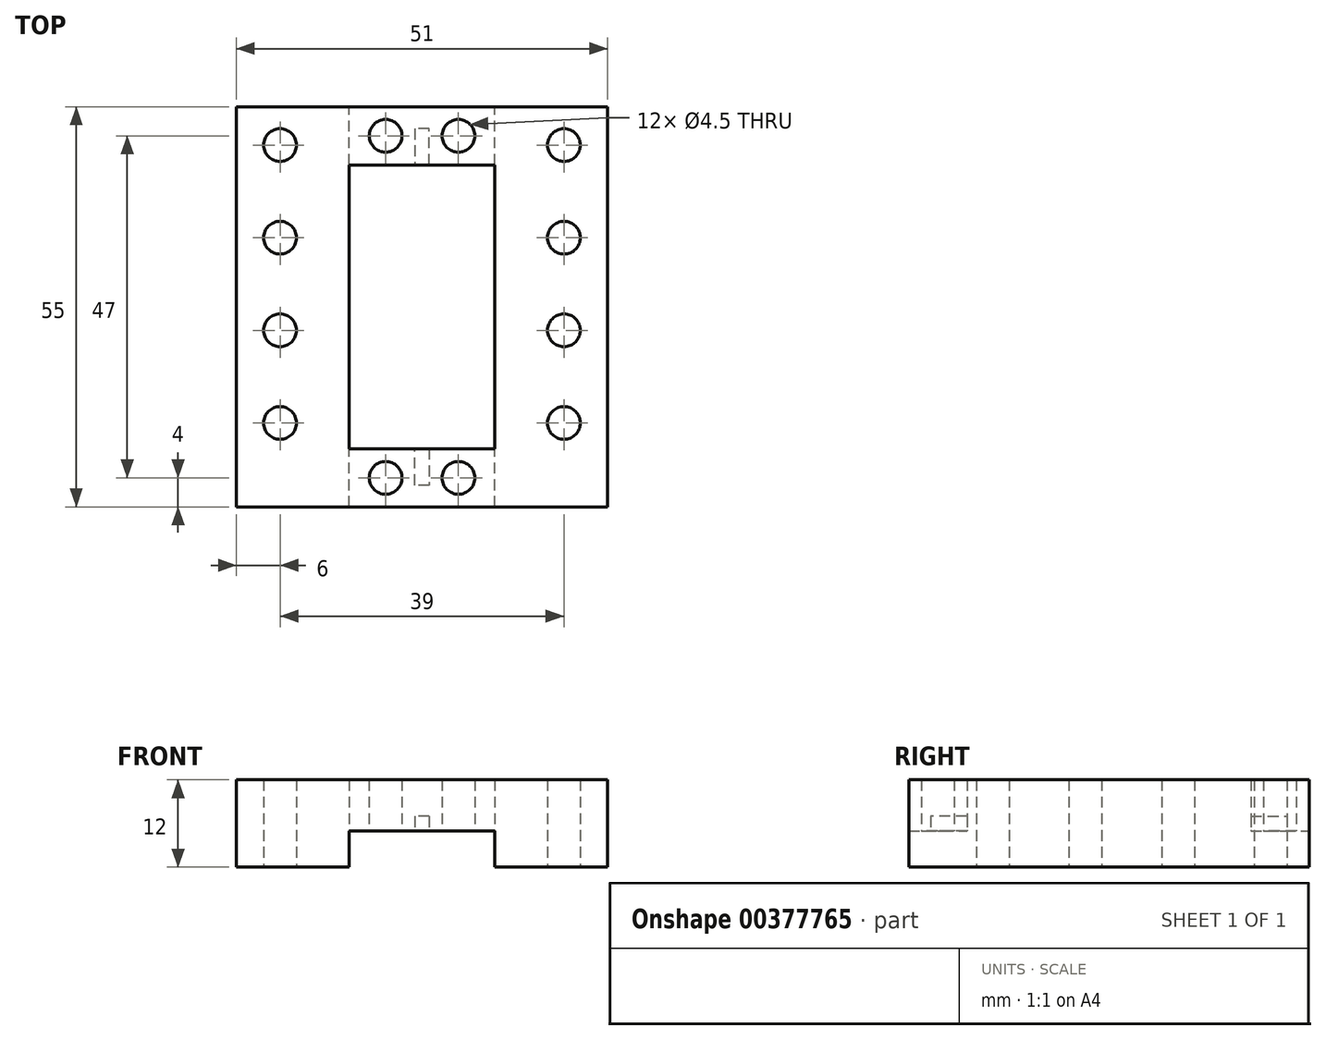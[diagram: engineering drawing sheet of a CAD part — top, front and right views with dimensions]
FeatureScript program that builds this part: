
annotation { "Feature Type Name" : "Feature", "Feature Type Description" : "" }
export const myFeature = defineFeature(function(context is Context, id is Id, definition is map)
    precondition{}
    {
        {
            var Q0;
            Q0=qCreatedBy(makeId("Top.planeOp"),FACE);
            var sketch = newSketch(context, id + "F0", { "sketchPlane" : qUnion([Q0])});
            skLineSegment(sketch, "E0.bottom", {"start": v(0, 0) * mm, "end": v(51, 0) * mm});
            skLineSegment(sketch, "E0.top", {"start": v(0, -55) * mm, "end": v(51, -55) * mm});
            skLineSegment(sketch, "E0.left", {"start": v(0, 0) * mm, "end": v(0, -55) * mm});
            skLineSegment(sketch, "E0.right", {"start": v(51, 0) * mm, "end": v(51, -55) * mm});
            skPoint(sketch, "E1", {"position": v(35.5, -55) * mm});
            skPoint(sketch, "E2", {"position": v(15.5, -55) * mm});
            skLineSegment(sketch, "E3", {"start": v(15.5, -55) * mm, "end": v(15.5, 0) * mm});
            skLineSegment(sketch, "E4", {"start": v(35.5, -55) * mm, "end": v(35.5, 0) * mm});
            skPoint(sketch, "E5", {"position": v(15.5, -47) * mm});
            skPoint(sketch, "E6", {"position": v(35.5, -47) * mm});
            skPoint(sketch, "E7", {"position": v(35.5, -8) * mm});
            skPoint(sketch, "E8", {"position": v(15.5, -8) * mm});
            skLineSegment(sketch, "E9", {"start": v(15.5, -47) * mm, "end": v(35.5, -47) * mm});
            skLineSegment(sketch, "E10", {"start": v(35.5, -8) * mm, "end": v(15.5, -8) * mm});
            skPoint(sketch, "E11", {"position": v(45, -55) * mm});
            skPoint(sketch, "E12", {"position": v(6, -55) * mm});
            skLineSegment(sketch, "E13", {"start": v(45, -55) * mm, "end": v(45, 0) * mm});
            skLineSegment(sketch, "E14", {"start": v(6, -55) * mm, "end": v(6, 0) * mm});
            skPoint(sketch, "E15", {"position": v(45, -18) * mm});
            skPoint(sketch, "E16", {"position": v(45, -30.73) * mm});
            skPoint(sketch, "E17", {"position": v(45, -5.27) * mm});
            skPoint(sketch, "E18", {"position": v(6, -18) * mm});
            skPoint(sketch, "E19", {"position": v(45, -43.46) * mm});
            skPoint(sketch, "E20", {"position": v(6, -43.46) * mm});
            skPoint(sketch, "E21", {"position": v(6, -30.73) * mm});
            skPoint(sketch, "E22", {"position": v(6, -5.27) * mm});
            skCircle(sketch, "E23", {"center": v(45, -43.46) * mm, "radius": 2.25 * mm});
            skCircle(sketch, "E24", {"center": v(45, -30.73) * mm, "radius": 2.25 * mm});
            skCircle(sketch, "E25", {"center": v(45, -18) * mm, "radius": 2.25 * mm});
            skCircle(sketch, "E26", {"center": v(45, -5.27) * mm, "radius": 2.25 * mm});
            skCircle(sketch, "E27", {"center": v(6, -43.46) * mm, "radius": 2.25 * mm});
            skCircle(sketch, "E28", {"center": v(6, -30.73) * mm, "radius": 2.25 * mm});
            skCircle(sketch, "E29", {"center": v(6, -18) * mm, "radius": 2.25 * mm});
            skCircle(sketch, "E30", {"center": v(6, -5.27) * mm, "radius": 2.25 * mm});
            skSolve(sketch);
        }
        {
            var Q0;
            {var subQ5=sQuery(id+"F0.wireOp",EDGE,"E10");Q0=makeQuery(id+"F0.imprint","IMPRINT",FACE,{"disambiguationData":[TD([[makeQuery(id+"F0.imprint","IMPRINT",EDGE,{"derivedFrom":subQ5}),-1.0]])]});}
            var Q1;
            {var subQ5=sQuery(id+"F0.wireOp",EDGE,"E9");Q1=makeQuery(id+"F0.imprint","IMPRINT",FACE,{"disambiguationData":[TD([[makeQuery(id+"F0.imprint","IMPRINT",EDGE,{"derivedFrom":subQ5}),-1.0]])]});}
            var Q2;
            {var subQ0=sQuery(id+"F0.wireOp",EDGE,"E0.left");Q2=makeQuery(id+"F0.imprint","IMPRINT",FACE,{"disambiguationData":[TD([[makeQuery(id+"F0.imprint","IMPRINT",EDGE,{"derivedFrom":subQ0}),1.0]])]});}
            var Q3;
            {var subQ4=sQuery(id+"F0.wireOp",EDGE,"E0.right");Q3=makeQuery(id+"F0.imprint","IMPRINT",FACE,{"disambiguationData":[TD([[makeQuery(id+"F0.imprint","IMPRINT",EDGE,{"derivedFrom":subQ4}),-1.0]])]});}
            var Q4;
            {var subQ1=sQuery(id+"F0.wireOp",EDGE,"E0.bottom");var subQ5=sQuery(id+"F0.wireOp",EDGE,"E3");var subQ6=makeQuery(id+"F0.imprint","INTERSECT",VERTEX,{"derivedFrom":[subQ1,subQ5]});Q4=makeQuery(id+"F0.imprint","IMPRINT",FACE,{"disambiguationData":[TD([[makeQuery(id+"F0.imprint","IMPRINT",EDGE,{"disambiguationData":[TD([[subQ6,1.0]])],"derivedFrom":subQ1}),-1.0]])]});}
            var Q5;
            {var subQ11=sQuery(id+"F0.wireOp",EDGE,"E0.bottom");var subQ15=sQuery(id+"F0.wireOp",EDGE,"E4");var subQ16=makeQuery(id+"F0.imprint","INTERSECT",VERTEX,{"derivedFrom":[subQ11,subQ15]});Q5=makeQuery(id+"F0.imprint","IMPRINT",FACE,{"disambiguationData":[TD([[makeQuery(id+"F0.imprint","IMPRINT",EDGE,{"disambiguationData":[TD([[subQ16,-1.0]])],"derivedFrom":subQ11}),-1.0]])]});}
            extrude(context, id + "F1", {"entities" : qUnion([Q0, Q1, Q2, Q3, Q4, Q5]), "depth" : 12 * mm});
        }
        {
            var Q0;
            {var subQ5=sQuery(id+"F0.wireOp",EDGE,"E9");Q0=makeQuery(id+"F0.imprint","IMPRINT",FACE,{"disambiguationData":[TD([[makeQuery(id+"F0.imprint","IMPRINT",EDGE,{"derivedFrom":subQ5}),-1.0]])]});}
            extrude(context, id + "F2", {"entities" : qUnion([Q0]), "operationType" : NewBodyOperationType.REMOVE, "depth" : 5 * mm});
        }
        {
            var Q0;
            {var subQ5=sQuery(id+"F0.wireOp",EDGE,"E10");Q0=makeQuery(id+"F0.imprint","IMPRINT",FACE,{"disambiguationData":[TD([[makeQuery(id+"F0.imprint","IMPRINT",EDGE,{"derivedFrom":subQ5}),-1.0]])]});}
            extrude(context, id + "F3", {"entities" : qUnion([Q0]), "operationType" : NewBodyOperationType.REMOVE, "depth" : 5 * mm});
        }
        {
            var Q0;
            Q0=makeQuery(id+"F2.boolean.opBoolean","COPY",FACE,{"derivedFrom":makeQuery(id+"F2.opExtrude","CAP_FACE",FACE,{"disambiguationData":[OSD([sQuery(id+"F0.wireOp",EDGE,"E0.top"),sQuery(id+"F0.wireOp",EDGE,"E3"),sQuery(id+"F0.wireOp",EDGE,"E4"),sQuery(id+"F0.wireOp",EDGE,"E9")])],"isStart":false})});
            var sketch = newSketch(context, id + "F4", { "sketchPlane" : qUnion([Q0])});
            skLineSegment(sketch, "E31", {"start": v(25.5, 47) * mm, "end": v(26.5, 47) * mm});
            skLineSegment(sketch, "E32", {"start": v(26.5, 47) * mm, "end": v(26.5, 52) * mm});
            skLineSegment(sketch, "E33", {"start": v(26.5, 52) * mm, "end": v(24.5, 52) * mm});
            skLineSegment(sketch, "E34", {"start": v(24.5, 52) * mm, "end": v(24.5, 47) * mm});
            skLineSegment(sketch, "E35", {"start": v(24.5, 47) * mm, "end": v(25.5, 47) * mm});
            skPoint(sketch, "E36", {"position": v(30.5, 55) * mm});
            skPoint(sketch, "E37", {"position": v(20.5, 55) * mm});
            skPoint(sketch, "E38", {"position": v(30.5, 51) * mm});
            skPoint(sketch, "E39", {"position": v(20.5, 51) * mm});
            skCircle(sketch, "E40", {"center": v(30.5, 51) * mm, "radius": 2.25 * mm});
            skCircle(sketch, "E41", {"center": v(20.5, 51) * mm, "radius": 2.25 * mm});
            skSolve(sketch);
        }
        {
            var Q0;
            Q0=makeQuery(id+"F4.imprint","IMPRINT",FACE,{"disambiguationData":[TD([[makeQuery(id+"F4.imprint","IMPRINT",EDGE,{"derivedFrom":sQuery(id+"F4.wireOp",EDGE,"E31")}),1.0]])]});
            extrude(context, id + "F5", {"entities" : qUnion([Q0]), "operationType" : NewBodyOperationType.REMOVE, "oppositeDirection" : true, "depth" : 2 * mm});
        }
        {
            var Q0;
            Q0=makeQuery(id+"F4.imprint","IMPRINT",FACE,{"disambiguationData":[TD([[makeQuery(id+"F4.imprint","IMPRINT",EDGE,{"derivedFrom":sQuery(id+"F4.wireOp",EDGE,"E41")}),1.0]])]});
            var Q1;
            Q1=makeQuery(id+"F4.imprint","IMPRINT",FACE,{"disambiguationData":[TD([[makeQuery(id+"F4.imprint","IMPRINT",EDGE,{"derivedFrom":sQuery(id+"F4.wireOp",EDGE,"E40")}),1.0]])]});
            extrude(context, id + "F6", {"entities" : qUnion([Q0, Q1]), "operationType" : NewBodyOperationType.REMOVE, "oppositeDirection" : true, "depth" : 25 * mm});
        }
        {
            var Q0;
            Q0=makeQuery(id+"F3.boolean.opBoolean","COPY",FACE,{"derivedFrom":makeQuery(id+"F3.opExtrude","CAP_FACE",FACE,{"disambiguationData":[OSD([sQuery(id+"F0.wireOp",EDGE,"E0.bottom"),sQuery(id+"F0.wireOp",EDGE,"E3"),sQuery(id+"F0.wireOp",EDGE,"E4"),sQuery(id+"F0.wireOp",EDGE,"E10")])],"isStart":false})});
            var sketch = newSketch(context, id + "F7", { "sketchPlane" : qUnion([Q0])});
            skLineSegment(sketch, "E42", {"start": v(25.5, 8) * mm, "end": v(26.5, 8) * mm});
            skLineSegment(sketch, "E43", {"start": v(26.5, 8) * mm, "end": v(26.5, 3) * mm});
            skLineSegment(sketch, "E44", {"start": v(26.5, 3) * mm, "end": v(24.5, 3) * mm});
            skLineSegment(sketch, "E45", {"start": v(24.5, 3) * mm, "end": v(24.5, 8) * mm});
            skLineSegment(sketch, "E46", {"start": v(24.5, 8) * mm, "end": v(25.5, 8) * mm});
            skPoint(sketch, "E47", {"position": v(30.5, 8) * mm});
            skPoint(sketch, "E48", {"position": v(20.5, 8) * mm});
            skPoint(sketch, "E49", {"position": v(30.5, 4) * mm});
            skPoint(sketch, "E50", {"position": v(20.5, 4) * mm});
            skCircle(sketch, "E51", {"center": v(20.5, 4) * mm, "radius": 2.25 * mm});
            skCircle(sketch, "E52", {"center": v(30.5, 4) * mm, "radius": 2.25 * mm});
            skSolve(sketch);
        }
        {
            var Q0;
            Q0=makeQuery(id+"F7.imprint","IMPRINT",FACE,{"disambiguationData":[TD([[makeQuery(id+"F7.imprint","IMPRINT",EDGE,{"derivedFrom":sQuery(id+"F7.wireOp",EDGE,"E42")}),1.0]])]});
            extrude(context, id + "F8", {"entities" : qUnion([Q0]), "operationType" : NewBodyOperationType.REMOVE, "oppositeDirection" : true, "depth" : 2 * mm});
        }
        {
            var Q0;
            Q0=makeQuery(id+"F7.imprint","IMPRINT",FACE,{"disambiguationData":[TD([[makeQuery(id+"F7.imprint","IMPRINT",EDGE,{"derivedFrom":sQuery(id+"F7.wireOp",EDGE,"E52")}),1.0]])]});
            var Q1;
            Q1=makeQuery(id+"F7.imprint","IMPRINT",FACE,{"disambiguationData":[TD([[makeQuery(id+"F7.imprint","IMPRINT",EDGE,{"derivedFrom":sQuery(id+"F7.wireOp",EDGE,"E51")}),1.0]])]});
            extrude(context, id + "F9", {"entities" : qUnion([Q0, Q1]), "operationType" : NewBodyOperationType.REMOVE, "oppositeDirection" : true, "depth" : 25 * mm});
        }
    });
